# Revit family: Kesselgruppe 2104
name_source: partatom
category: Rohrzubehör
units: mm (PartAtom-declared; Revit-internal decimal feet)

## family parameters
Arbeitsebenenbasiert = Nein
Beim Laden mit Abzugskörper schneiden = Nein
Bemaßung runder Anschluss = Durchmesser verwenden
Gemeinsam genutzt = Nein
Immer vertikal = Ja
OmniClass-Nummer = 23.65.55.14
OmniClass-Titel = Valves for Liquid Services
Teiletyp = Normal

## types (1)
- Kesselgruppe 2104
    Entlüfter = geschmiedetes Messing nach EN 12165; CW617N
    Gewicht = 0.663
    Hersteller = Herz-Armaturen GmbH
    L01 = 72 mm
    L02 = 27 mm  [stored 0.0885827 ft]
    L03 = 52.4 mm  [stored 0.171916 ft]
    L04 = 30.6 mm  [stored 0.100394 ft]
    L05 = 19.4 mm  [stored 0.0636483 ft]
    L06 = 34.4 mm  [stored 0.112861 ft]
    L07 = 27.7 mm  [stored 0.0908793 ft]
    L08 = 37.2 mm  [stored 0.122047 ft]
    L09 = 20.7 mm  [stored 0.0679134 ft]
    L10 = 86 mm
    L11 = 31.2 mm  [stored 0.102362 ft]
    L12 = 29.5 mm
    L13 = 46.5 mm  [stored 0.152559 ft]
    L14 = 31.5 mm  [stored 0.103346 ft]
    L15 = 47.8 mm  [stored 0.156824 ft]
    L16 = 21.4 mm  [stored 0.07021 ft]
    L17 = 95.3 mm
    L18 = 73.3 mm
    L19 = 22 mm  [stored 0.0721785 ft]
    Manometer = 0 bis 4 bar
    Medium = Heizungswasser nach ÖNORM H5195 oder VDI- Richtlinie 2035. Die Verwendung von Ethylen- oder Propyleneglykol in einem Mischungsverhältnis 25- 50% ist zulässig. EPDM-Dichtungen können durch Mineralöle und Schmiermittel beeinflusst werden, was zum Versagen der EPDM-Dichtungen führen kann. Bitte beachten Sie die Dokumentation des Herstellers, wenn Ethylenglykol-Produkte für den Frost- und Korrosionsschutz verwendet werden.
    Nennweite SV = 20 mm  [stored 0.0656168 ft]
    R01 = 41.5 mm  [stored 0.136155 ft]
    R02 = 39.9 mm  [stored 0.130906 ft]
    R03 = 12.7 mm  [stored 0.0416667 ft]
    R04 = 10.65 mm  [stored 0.0349409 ft]
    R05 = 13 mm
    R06 = 9.3 mm  [stored 0.0305118 ft]
    R07 = 9.5 mm  [stored 0.031168 ft]
    R08 = 10.65 mm  [stored 0.0349409 ft]
    R09 = 13 mm
    R10 = 10.65 mm  [stored 0.0349409 ft]
    R11 = 12.5 mm  [stored 0.0410105 ft]
    R12 = 17.1 mm  [stored 0.0561024 ft]
    R13 = 17.9 mm
    R14 = 10.65 mm  [stored 0.0349409 ft]
    R16 = 12 mm  [stored 0.0393701 ft]
    R17 = 20.8 mm  [stored 0.0682415 ft]
    R18 = 10 mm  [stored 0.0328084 ft]
    R19 = 16 mm  [stored 0.0524934 ft]
    R20 = 9.3 mm  [stored 0.0305118 ft]
    R21 = 14.8 mm  [stored 0.0485564 ft]
    R22 = 12.3 mm
    R23 = 10.4 mm  [stored 0.0341207 ft]
    R24 = 13.9 mm  [stored 0.0456037 ft]
    R25 = 10.4 mm  [stored 0.0341207 ft]
    S01 = 31.8 mm  [stored 0.104331 ft]
    S02 = 95.3 mm
    S03 = 45 mm  [stored 0.147638 ft]
    S04 = 32 mm  [stored 0.104987 ft]
    S05 = 71 mm
    S06 = 42.7 mm  [stored 0.140092 ft]
    S07 = 69.9 mm
    S08 = 17.7 mm  [stored 0.0580709 ft]
    SCRNCODE = 02;04;02
    SCRNSEQ = AWI;AWI_TYP="1001";2
    Sicherheitsventil = geschmiedetes Messing nach EN 12165; CW617N
    URL = www.herz-armaturen.at
    Verbindungsstück = geschmiedetes Messing nach EN 12165; CW617N
    Vorgabe-Ansicht = 0 mm  [stored 0 ft]
    Wäremdämmung = EPP
    max.Betriebstemperatur = 110 °C
    min.Betriebstemperatur = -10 °C
    Öffnungsdruck = 300000.0 Pa

note: [stored X ft] marks values corroborated as IEEE doubles in the binary element streams (Revit-internal decimal feet)
